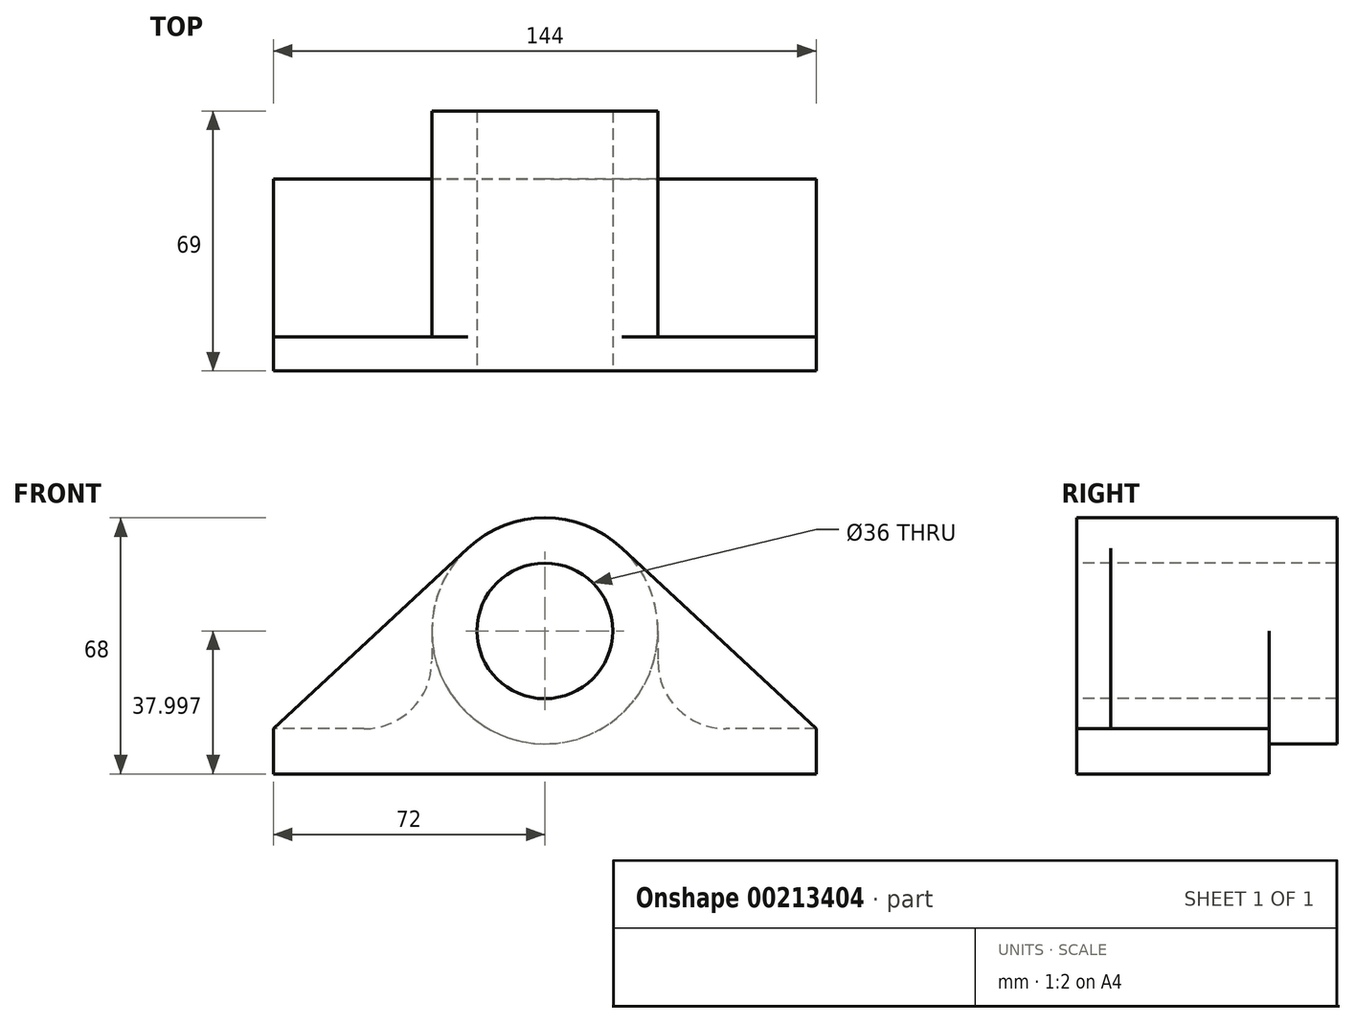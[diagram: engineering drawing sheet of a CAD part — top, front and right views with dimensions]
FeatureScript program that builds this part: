
annotation { "Feature Type Name" : "Feature", "Feature Type Description" : "" }
export const myFeature = defineFeature(function(context is Context, id is Id, definition is map)
    precondition{}
    {
        {
            var Q0;
            Q0=qCreatedBy(makeId("Front.planeOp"),FACE);
            var sketch = newSketch(context, id + "F0", { "sketchPlane" : qUnion([Q0])});
            skLineSegment(sketch, "E0.top", {"start": v(-67.1, -51.35) * mm, "end": v(76.9, -51.35) * mm});
            skLineSegment(sketch, "E0.left", {"start": v(-67.1, -39.35) * mm, "end": v(-67.1, -51.35) * mm});
            skLineSegment(sketch, "E0.right", {"start": v(76.9, -39.35) * mm, "end": v(76.9, -51.35) * mm});
            skCircle(sketch, "E1", {"center": v(4.9, -13.35) * mm, "radius": 18 * mm});
            skCircle(sketch, "E2", {"center": v(4.9, -13.35) * mm, "radius": 30 * mm});
            skLineSegment(sketch, "E3", {"start": v(-67.1, -39.35) * mm, "end": v(-15.54, 8.61) * mm});
            skLineSegment(sketch, "E4", {"start": v(25.32, 8.61) * mm, "end": v(76.9, -39.35) * mm});
            skSolve(sketch);
        }
        {
            var Q0;
            Q0=qSketchRegion(id+"F0",true);
            var Q1;
            Q1=makeQuery(id+"F0.imprint","IMPRINT",FACE,{"disambiguationData":[TD([[makeQuery(id+"F0.imprint","IMPRINT",EDGE,{"derivedFrom":sQuery(id+"F0.wireOp",EDGE,"E0.top")}),1.0]])]});
            extrude(context, id + "F1", {"entities" : qUnion([Q0, Q1]), "oppositeDirection" : true, "depth" : 9 * mm});
        }
        {
            var Q0;
            Q0=makeQuery(id+"F1.opExtrude","CAP_FACE",FACE,{"disambiguationData":[OSD([sQuery(id+"F0.wireOp",EDGE,"E0.top"),sQuery(id+"F0.wireOp",EDGE,"E0.left"),sQuery(id+"F0.wireOp",EDGE,"E0.right"),sQuery(id+"F0.wireOp",EDGE,"E1"),sQuery(id+"F0.wireOp",EDGE,"E2"),sQuery(id+"F0.wireOp",EDGE,"E3"),sQuery(id+"F0.wireOp",EDGE,"E4")])],"isStart":false});
            var sketch = newSketch(context, id + "F2", { "sketchPlane" : qUnion([Q0])});
            skCircle(sketch, "E5", {"center": v(-4.9, -13.35) * mm, "radius": 18 * mm});
            skCircle(sketch, "E6", {"center": v(-4.9, -13.35) * mm, "radius": 30 * mm});
            skSolve(sketch);
        }
        {
            var Q0;
            Q0=qSketchRegion(id+"F2",true);
            var Q1;
            Q1=makeQuery(id+"F2.imprint","IMPRINT",FACE,{"disambiguationData":[TD([[makeQuery(id+"F2.imprint","IMPRINT",EDGE,{"derivedFrom":sQuery(id+"F2.wireOp",EDGE,"E5")}),1.0]])]});
            extrude(context, id + "F3", {"entities" : qUnion([Q0, Q1]), "operationType" : NewBodyOperationType.ADD, "depth" : 60 * mm});
        }
        {
            var Q0;
            Q0=makeQuery(id+"F1.opExtrude","CAP_FACE",FACE,{"disambiguationData":[OSD([sQuery(id+"F0.wireOp",EDGE,"E0.top"),sQuery(id+"F0.wireOp",EDGE,"E0.left"),sQuery(id+"F0.wireOp",EDGE,"E0.right"),sQuery(id+"F0.wireOp",EDGE,"E1"),sQuery(id+"F0.wireOp",EDGE,"E2"),sQuery(id+"F0.wireOp",EDGE,"E3"),sQuery(id+"F0.wireOp",EDGE,"E4")])],"isStart":false});
            var sketch = newSketch(context, id + "F4", { "sketchPlane" : qUnion([Q0])});
            skLineSegment(sketch, "E7.bottom", {"start": v(-76.9, -51.35) * mm, "end": v(67.1, -51.35) * mm});
            skLineSegment(sketch, "E7.top", {"start": v(-76.9, -51.35) * mm, "end": v(67.1, -51.35) * mm});
            skLineSegment(sketch, "E7.left", {"start": v(-76.9, -51.35) * mm, "end": v(-76.9, -51.35) * mm});
            skLineSegment(sketch, "E7.right", {"start": v(67.1, -51.35) * mm, "end": v(67.1, -51.35) * mm});
            skLineSegment(sketch, "E8.bottom", {"start": v(43.1, -39.35) * mm, "end": v(67.1, -39.35) * mm});
            skLineSegment(sketch, "E8.top", {"start": v(-76.9, -39.32) * mm, "end": v(-52.9, -39.32) * mm});
            skLineSegment(sketch, "E8.left", {"start": v(-76.9, -39.35) * mm, "end": v(-76.9, -39.32) * mm});
            skLineSegment(sketch, "E8.right", {"start": v(67.1, -39.35) * mm, "end": v(67.1, -39.35) * mm});
            skLineSegment(sketch, "E9.left", {"start": v(67.1, -51.35) * mm, "end": v(67.1, -39.35) * mm});
            skLineSegment(sketch, "E9.right", {"start": v(67.1, -51.35) * mm, "end": v(67.1, -39.35) * mm});
            skLineSegment(sketch, "E10.bottom", {"start": v(-76.9, -45.35) * mm, "end": v(-76.9, -45.35) * mm});
            skLineSegment(sketch, "E10.left", {"start": v(-76.9, -45.35) * mm, "end": v(-76.9, -51.35) * mm});
            skLineSegment(sketch, "E10.right", {"start": v(-76.9, -45.35) * mm, "end": v(-76.9, -51.35) * mm});
            skArc(sketch, "E11", {"start": v(-34.9, -13.35) * mm, "mid": v(-4.9, -43.35) * mm, "end": v(25.1, -13.35) * mm});
            skArc(sketch, "E12", {"start": v(13.1, -13.35) * mm, "mid": v(-4.9, -31.35) * mm, "end": v(-22.9, -13.35) * mm});
            skLineSegment(sketch, "E13", {"start": v(-34.9, -13.35) * mm, "end": v(-22.9, -13.35) * mm});
            skLineSegment(sketch, "E14", {"start": v(13.1, -13.35) * mm, "end": v(25.1, -13.35) * mm});
            skLineSegment(sketch, "E15", {"start": v(-34.9, -13.35) * mm, "end": v(-34.9, -21.32) * mm});
            skArc(sketch, "E16.filletArc", {"start": v(-52.9, -39.32) * mm, "mid": v(-40.16, -34.05) * mm, "end": v(-34.9, -21.32) * mm});
            skLineSegment(sketch, "E17", {"start": v(25.1, -13.35) * mm, "end": v(25.1, -21.35) * mm});
            skArc(sketch, "E18.filletArc", {"start": v(25.1, -21.35) * mm, "mid": v(30.38, -34.08) * mm, "end": v(43.1, -39.35) * mm});
            skLineSegment(sketch, "E19", {"start": v(-76.9, -39.32) * mm, "end": v(-76.9, -45.35) * mm});
            skSolve(sketch);
        }
        {
            var Q0;
            Q0=qSketchRegion(id+"F4",true);
            extrude(context, id + "F5", {"entities" : qUnion([Q0]), "operationType" : NewBodyOperationType.ADD, "depth" : 42 * mm});
        }
    });
